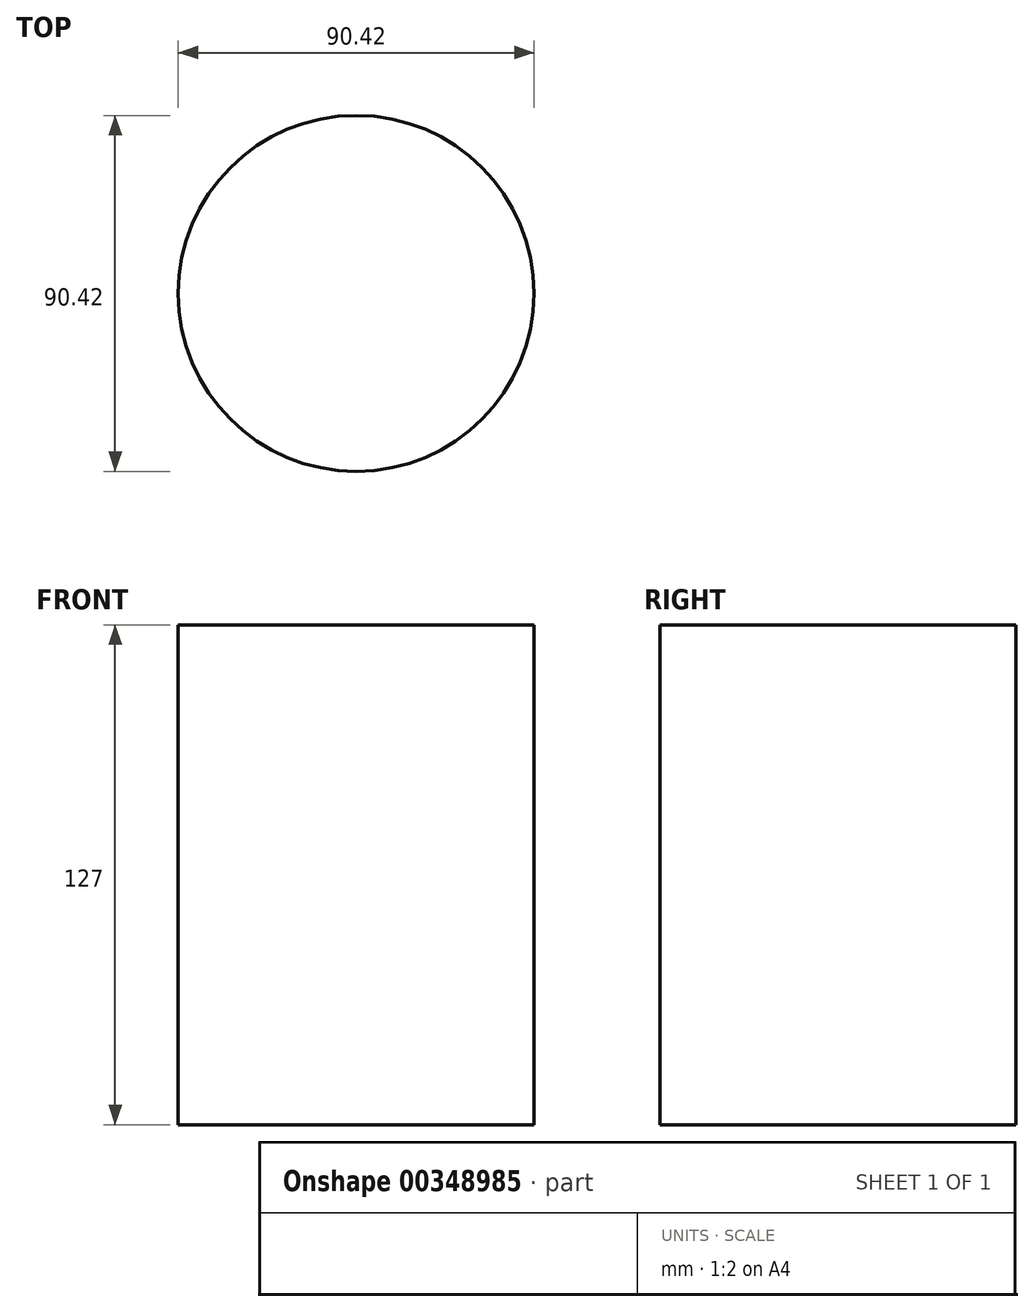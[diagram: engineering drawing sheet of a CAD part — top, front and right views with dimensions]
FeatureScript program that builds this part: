
annotation { "Feature Type Name" : "Feature", "Feature Type Description" : "" }
export const myFeature = defineFeature(function(context is Context, id is Id, definition is map)
    precondition{}
    {
        {
            var Q0;
            Q0=qCreatedBy(makeId("Top.planeOp"),FACE);
            var sketch = newSketch(context, id + "F0", { "sketchPlane" : qUnion([Q0])});
            skCircle(sketch, "E0", {"center": v(0, 0) * mm, "radius": 45.21 * mm});
            skSolve(sketch);
        }
        {
            var Q0;
            Q0=makeQuery(id+"F0.imprint","IMPRINT",FACE,{"disambiguationData":[TD([[makeQuery(id+"F0.imprint","IMPRINT",EDGE,{"derivedFrom":sQuery(id+"F0.wireOp",EDGE,"E0")}),1.0]])]});
            extrude(context, id + "F1", {"entities" : qUnion([Q0]), "depth" : 127 * mm});
        }
    });
